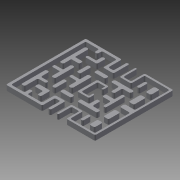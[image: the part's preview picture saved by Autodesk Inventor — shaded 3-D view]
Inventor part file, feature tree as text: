
AUTODESK INVENTOR PART (.ipt)
format: ipt  version: 2015 (Build 190159000, 159)  size: 590,336 bytes
history: native  units: in
note: dims shown in document units (in); Inventor stores cm internally (conversion verified against a paired STEP export)
features: fillet x4, extrude x1, sketch x1, other x1
ambient origin geometry x8: Origin, YZ Plane, XZ Plane, XY Plane, X Axis, Y Axis, Z Axis, Center Point
bodies: Solid1 (feature_tree)
feature tree (7):
  extrude  "Extrusion1"  Depth=0.0625in
  fillet  "Fillet1"  Radius=0.0625in
  fillet  "Fillet2"  Radius=0.0625in
  fillet  "Fillet3"  Radius=0.0625in
  fillet  "Fillet4"  [1 undecoded]
  sketch  "Sketch1"  dims[d11=0.25in d12=0.0in d13=0.0625in d14=0.0625in d15=0.0625in d16=0.0625in]
  other  "Image1"
note: 1 required parameter value undecoded (feature->parameter linkage not recoverable at this tier; creation-order binding heuristic only, values carry confidence <= 0.55)
